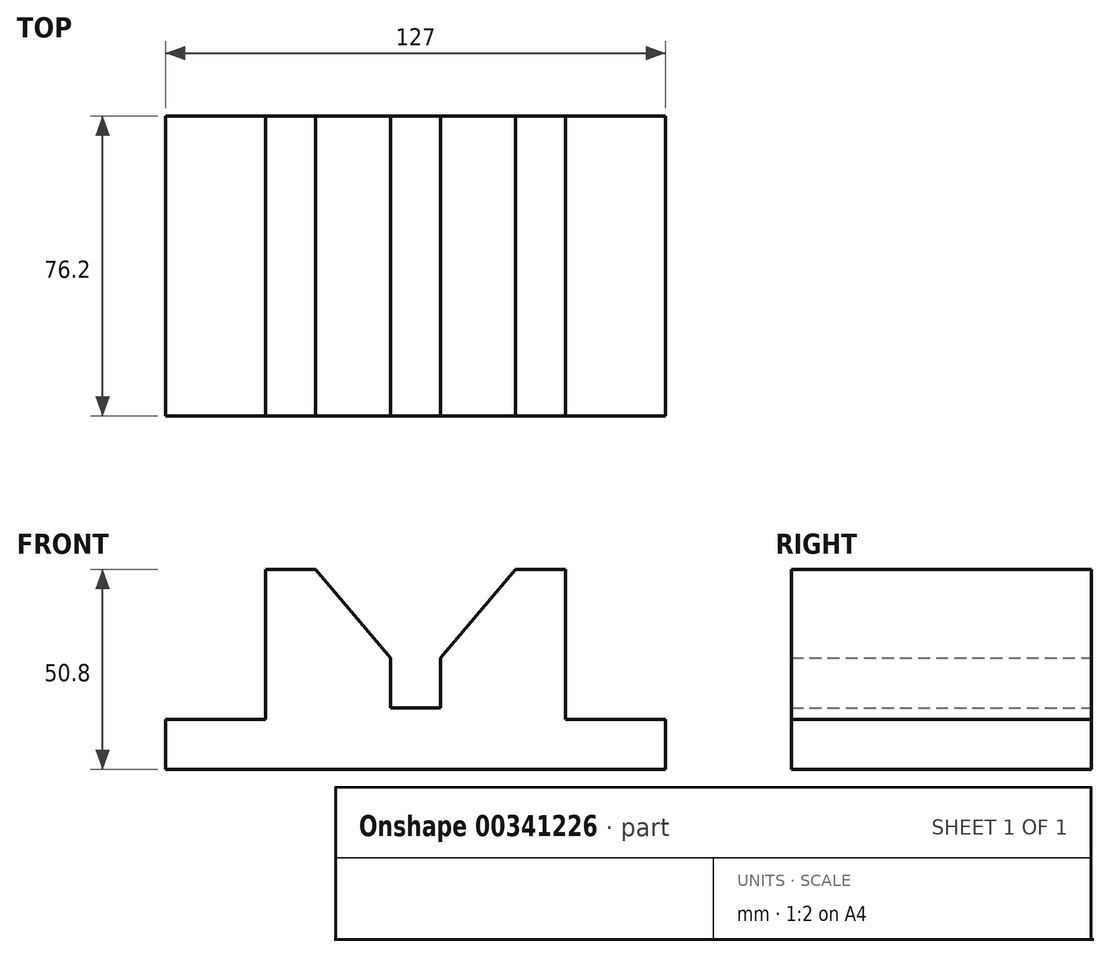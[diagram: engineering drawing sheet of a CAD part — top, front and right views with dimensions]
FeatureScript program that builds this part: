
annotation { "Feature Type Name" : "Feature", "Feature Type Description" : "" }
export const myFeature = defineFeature(function(context is Context, id is Id, definition is map)
    precondition{}
    {
        {
            var Q0;
            Q0=qCreatedBy(makeId("Front.planeOp"),FACE);
            var sketch = newSketch(context, id + "F0", { "sketchPlane" : qUnion([Q0])});
            skLineSegment(sketch, "E0", {"start": v(0, 0) * mm, "end": v(0, 12.7) * mm});
            skLineSegment(sketch, "E1", {"start": v(0, 12.7) * mm, "end": v(25.4, 12.7) * mm});
            skLineSegment(sketch, "E2", {"start": v(25.4, 12.7) * mm, "end": v(25.4, 50.8) * mm});
            skLineSegment(sketch, "E3", {"start": v(25.4, 50.8) * mm, "end": v(38.1, 50.8) * mm});
            skLineSegment(sketch, "E4", {"start": v(38.1, 50.8) * mm, "end": v(57.15, 28.35) * mm});
            skLineSegment(sketch, "E5", {"start": v(57.15, 28.35) * mm, "end": v(57.15, 15.65) * mm});
            skLineSegment(sketch, "E6", {"start": v(57.15, 15.65) * mm, "end": v(69.85, 15.65) * mm});
            skLineSegment(sketch, "E7", {"start": v(69.85, 15.65) * mm, "end": v(69.85, 28.35) * mm});
            skLineSegment(sketch, "E8", {"start": v(69.85, 28.35) * mm, "end": v(88.9, 50.8) * mm});
            skLineSegment(sketch, "E9", {"start": v(88.9, 50.8) * mm, "end": v(101.6, 50.8) * mm});
            skLineSegment(sketch, "E10", {"start": v(101.6, 50.8) * mm, "end": v(101.6, 12.7) * mm});
            skLineSegment(sketch, "E11", {"start": v(101.6, 12.7) * mm, "end": v(127, 12.7) * mm});
            skLineSegment(sketch, "E12", {"start": v(127, 12.7) * mm, "end": v(127, 0) * mm});
            skLineSegment(sketch, "E13", {"start": v(127, 0) * mm, "end": v(0, 0) * mm});
            skSolve(sketch);
        }
        {
            var Q0;
            Q0 = qSketchRegion(id + "F0", true);
            extrude(context, id + "F1", {"entities" : qUnion([Q0]), "depth" : 76.2 * mm});
        }
    });
